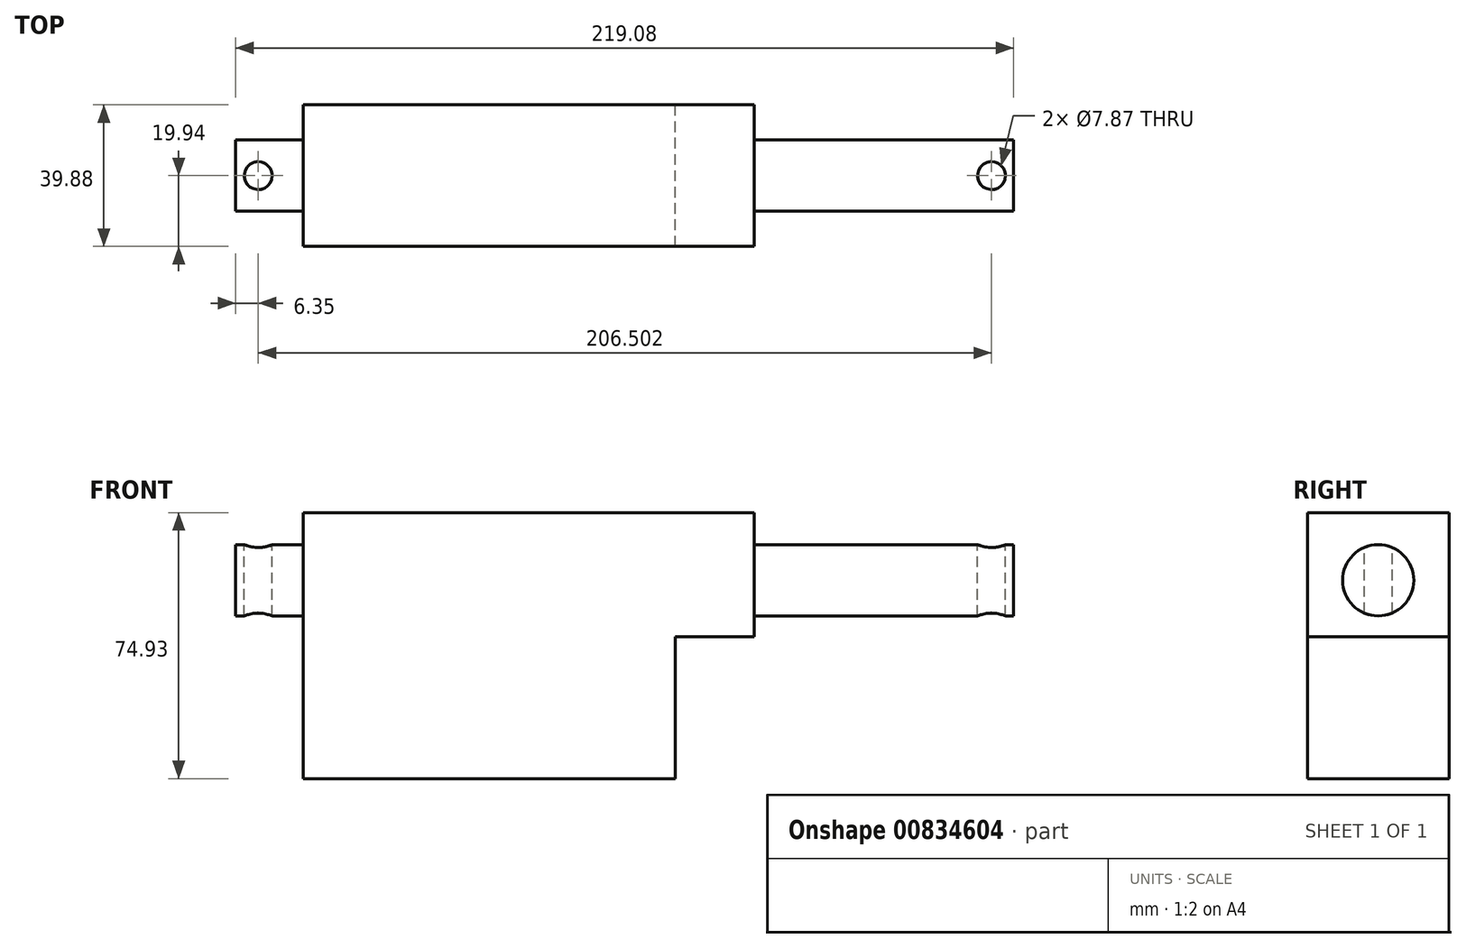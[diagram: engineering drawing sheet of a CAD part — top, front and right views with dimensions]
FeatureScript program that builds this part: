
annotation { "Feature Type Name" : "Feature", "Feature Type Description" : "" }
export const myFeature = defineFeature(function(context is Context, id is Id, definition is map)
    precondition{}
    {
        {
            var Q0;
            Q0=qCreatedBy(makeId("Right.planeOp"),FACE);
            var sketch = newSketch(context, id + "F0", { "sketchPlane" : qUnion([Q0])});
            skCircle(sketch, "E0", {"center": v(0, 0) * mm, "radius": 10.03 * mm});
            skSolve(sketch);
        }
        {
            var Q0;
            Q0=qSketchRegion(id+"F0",true);
            extrude(context, id + "F1", {"entities" : qUnion([Q0]), "depth" : 219.07 * mm, "offsetDistance" : 25.4 * mm});
        }
        {
            var Q0;
            Q0=qCreatedBy(makeId("Right.planeOp"),FACE);
            cPlane(context, id + "F2", {"entities" : qUnion([Q0]), "cplaneType" : CPlaneType.OFFSET, "offset" : 19.05 * mm, "width" : 152.4 * mm, "height" : 152.4 * mm});
        }
        {
            var Q0;
            Q0=qCreatedBy(id+"F2.planeOp",FACE);
            var sketch = newSketch(context, id + "F3", { "sketchPlane" : qUnion([Q0])});
            skLineSegment(sketch, "E1.bottom", {"start": v(-19.94, 19.05) * mm, "end": v(19.94, 19.05) * mm});
            skLineSegment(sketch, "E1.top", {"start": v(-19.94, -55.88) * mm, "end": v(19.94, -55.88) * mm});
            skLineSegment(sketch, "E1.left", {"start": v(-19.94, 19.05) * mm, "end": v(-19.94, -55.88) * mm});
            skLineSegment(sketch, "E1.right", {"start": v(19.94, 19.05) * mm, "end": v(19.94, -55.88) * mm});
            skSolve(sketch);
        }
        {
            var Q0;
            Q0=makeQuery(id+"F3.imprint","IMPRINT",FACE,{"disambiguationData":[TD([[makeQuery(id+"F3.imprint","IMPRINT",EDGE,{"derivedFrom":sQuery(id+"F3.wireOp",EDGE,"E1.bottom")}),-1.0]])]});
            extrude(context, id + "F4", {"entities" : qUnion([Q0]), "operationType" : NewBodyOperationType.ADD, "depth" : 127 * mm, "offsetDistance" : 25.4 * mm});
        }
        {
            var Q0;
            Q0=makeQuery(id+"F4.opExtrude","CAP_FACE",FACE,{"disambiguationData":[OSD([sQuery(id+"F3.wireOp",EDGE,"E1.bottom"),sQuery(id+"F3.wireOp",EDGE,"E1.top"),sQuery(id+"F3.wireOp",EDGE,"E1.left"),sQuery(id+"F3.wireOp",EDGE,"E1.right")])],"isStart":false});
            var sketch = newSketch(context, id + "F5", { "sketchPlane" : qUnion([Q0])});
            skLineSegment(sketch, "E2.bottom", {"start": v(-19.94, -55.88) * mm, "end": v(19.94, -55.88) * mm});
            skLineSegment(sketch, "E2.top", {"start": v(-19.94, -15.88) * mm, "end": v(19.94, -15.88) * mm});
            skLineSegment(sketch, "E2.left", {"start": v(-19.94, -55.88) * mm, "end": v(-19.94, -15.88) * mm});
            skLineSegment(sketch, "E2.right", {"start": v(19.94, -55.88) * mm, "end": v(19.94, -15.88) * mm});
            skSolve(sketch);
        }
        {
            var Q0;
            Q0=makeQuery(id+"F5.imprint","IMPRINT",FACE,{"disambiguationData":[TD([[makeQuery(id+"F5.imprint","IMPRINT",EDGE,{"derivedFrom":sQuery(id+"F5.wireOp",EDGE,"E2.bottom")}),1.0]])]});
            extrude(context, id + "F6", {"entities" : qUnion([Q0]), "operationType" : NewBodyOperationType.REMOVE, "oppositeDirection" : true, "depth" : 22.22 * mm, "offsetDistance" : 25.4 * mm});
        }
        {
            var Q0;
            Q0=qCreatedBy(makeId("Top.planeOp"),FACE);
            var sketch = newSketch(context, id + "F7", { "sketchPlane" : qUnion([Q0])});
            skCircle(sketch, "E3", {"center": v(6.35, 0) * mm, "radius": 3.94 * mm});
            skCircle(sketch, "E4", {"center": v(212.85, 0) * mm, "radius": 3.94 * mm});
            skSolve(sketch);
        }
        {
            var Q0;
            Q0 = qSketchRegion(id + "F7", true);
            extrude(context, id + "F8", {"entities" : qUnion([Q0]), "operationType" : NewBodyOperationType.REMOVE, "endBound" : BoundingType.THROUGH_ALL, "oppositeDirection" : true, "depth" : 25.4 * mm, "offsetDistance" : 25.4 * mm, "hasSecondDirection" : true, "secondDirectionBound" : SecondDirectionBoundingType.THROUGH_ALL, "secondDirectionOppositeDirection" : false, "secondDirectionDepth" : 25.4 * mm});
        }
    });
